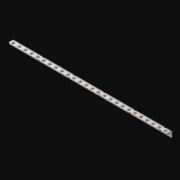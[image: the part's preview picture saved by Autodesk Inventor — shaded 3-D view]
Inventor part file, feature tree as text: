
AUTODESK INVENTOR PART (.ipt)
format: ipt  version: 2021 (Build 250183000, 183)  size: 785,408 bytes
history: native  units: in
note: dims shown in document units (in); Inventor stores cm internally (conversion verified against a paired STEP export)
features: extrude x53, other x52, sketch x3, pattern_linear x1, sheet_metal_op x1
ambient origin geometry x8: Origin, YZ Plane, XZ Plane, XY Plane, X Axis, Y Axis, Z Axis, Center Point
bodies: Solid1 (feature_tree)
feature tree (110):
  pattern_linear  "Rectangular Pattern1"  Spacing1=0.063in  [1 undecoded]
  extrude  "Extrusion1"  Depth=0.5in
  sketch  "Sketch1"  dims[d0=0.182in]
  other  "Srf1"
  sketch  "Sketch2"  dims[d1=0.063in d2=0.0in]
  other  "Srf2"
  other  "Srf3"
  other  "Srf5"
  other  "Srf7"
  other  "Srf9"
  other  "Srf11"
  other  "Srf13"
  other  "Srf15"
  other  "Srf17"
  other  "Srf19"
  other  "Srf21"
  other  "Srf23"
  other  "Srf25"
  other  "Srf27"
  other  "Srf29"
  other  "Srf31"
  other  "Srf33"
  other  "Srf35"
  other  "Srf37"
  other  "Srf39"
  other  "Srf41"
  other  "Srf43"
  other  "Srf45"
  other  "Srf47"
  other  "Srf49"
  other  "Srf51"
  other  "Srf4"
  other  "Srf6"
  other  "Srf8"
  other  "Srf10"
  other  "Srf12"
  other  "Srf14"
  other  "Srf16"
  other  "Srf18"
  other  "Srf20"
  other  "Srf22"
  other  "Srf24"
  other  "Srf26"
  other  "Srf28"
  other  "Srf30"
  other  "Srf32"
  other  "Srf34"
  other  "Srf36"
  other  "Srf38"
  other  "Srf40"
  other  "Srf42"
  other  "Srf44"
  other  "Srf46"
  other  "Srf48"
  other  "Srf50"
  other  "Srf52"
  sketch  "Sketch3"  dims[d3=0.182in d4=0.063in d5=0.0in d8=0.5in d9=4.5in d10=0.0in]
  sheet_metal_op  "Fold1"
  extrude  "ExtrusionSrf1"  Depth=4.5in TaperAngle=0.0deg
  extrude  "ExtrusionSrf2"  [1 undecoded]
  extrude  "ExtrusionSrf3"  [1 undecoded]
  extrude  "ExtrusionSrf4"  [1 undecoded]
  extrude  "ExtrusionSrf5"  [1 undecoded]
  extrude  "ExtrusionSrf6"  [1 undecoded]
  extrude  "ExtrusionSrf7"  [1 undecoded]
  extrude  "ExtrusionSrf8"  [1 undecoded]
  extrude  "ExtrusionSrf9"  [1 undecoded]
  extrude  "ExtrusionSrf10"  [1 undecoded]
  extrude  "ExtrusionSrf11"  [1 undecoded]
  extrude  "ExtrusionSrf12"  [1 undecoded]
  extrude  "ExtrusionSrf13"  [1 undecoded]
  extrude  "ExtrusionSrf14"  [1 undecoded]
  extrude  "ExtrusionSrf15"  [1 undecoded]
  extrude  "ExtrusionSrf16"  [1 undecoded]
  extrude  "ExtrusionSrf17"  [1 undecoded]
  extrude  "ExtrusionSrf18"  [1 undecoded]
  extrude  "ExtrusionSrf19"  [1 undecoded]
  extrude  "ExtrusionSrf20"  [1 undecoded]
  extrude  "ExtrusionSrf21"  [1 undecoded]
  extrude  "ExtrusionSrf22"  [1 undecoded]
  extrude  "ExtrusionSrf23"  [1 undecoded]
  extrude  "ExtrusionSrf24"  [1 undecoded]
  extrude  "ExtrusionSrf25"  [1 undecoded]
  extrude  "ExtrusionSrf26"  [1 undecoded]
  extrude  "ExtrusionSrf27"  [1 undecoded]
  extrude  "ExtrusionSrf37"  [1 undecoded]
  extrude  "ExtrusionSrf38"  [1 undecoded]
  extrude  "ExtrusionSrf39"  [1 undecoded]
  extrude  "ExtrusionSrf40"  [1 undecoded]
  extrude  "ExtrusionSrf41"  [1 undecoded]
  extrude  "ExtrusionSrf42"  [1 undecoded]
  extrude  "ExtrusionSrf43"  [1 undecoded]
  extrude  "ExtrusionSrf44"  [1 undecoded]
  extrude  "ExtrusionSrf45"  [1 undecoded]
  extrude  "ExtrusionSrf46"  [1 undecoded]
  extrude  "ExtrusionSrf47"  [1 undecoded]
  extrude  "ExtrusionSrf48"  [1 undecoded]
  extrude  "ExtrusionSrf49"  [1 undecoded]
  extrude  "ExtrusionSrf50"  [1 undecoded]
  extrude  "ExtrusionSrf51"  [1 undecoded]
  extrude  "ExtrusionSrf52"  [1 undecoded]
  extrude  "ExtrusionSrf53"  [1 undecoded]
  extrude  "ExtrusionSrf54"  [1 undecoded]
  extrude  "ExtrusionSrf55"  [1 undecoded]
  extrude  "ExtrusionSrf56"  [1 undecoded]
  extrude  "ExtrusionSrf57"  [1 undecoded]
  extrude  "ExtrusionSrf58"  [1 undecoded]
  extrude  "ExtrusionSrf59"  [1 undecoded]
  extrude  "ExtrusionSrf60"  [1 undecoded]
  extrude  "ExtrusionSrf61"  [1 undecoded]
note: 52 required parameter values undecoded (feature->parameter linkage not recoverable at this tier; creation-order binding heuristic only, values carry confidence <= 0.55)
